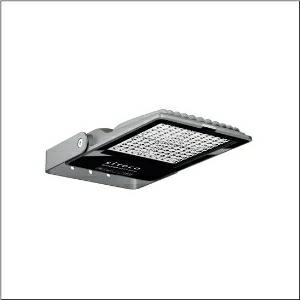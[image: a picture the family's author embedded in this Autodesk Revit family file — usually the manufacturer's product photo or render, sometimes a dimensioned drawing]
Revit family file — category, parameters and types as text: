
# Revit family: sicompact_r__31_mini___pl32_5xa7571b2k23_8fae
name_source: partatom
category: Lighting Fixtures
units: mm (PartAtom-declared; Revit-internal decimal feet)

## family parameters
Cut with Voids When Loaded = No
Host = Face
Light Source = No
Part Type = Normal
Room Calculation Point = No
Round Connector Dimension = Use Diameter
Shared = No

## types (1)
- SiCompact® 31 mini  PL32 (1 x LED, 8000 lm, 47 W, 4000K)
    Apparent Load = 47 VA
    CIE Flux Codes = 32 69 98 100 100
    Color Rendering = 70
    Color Temperature = 4000K
    Default Elevation = 1800 mm
    Description = SiCompact® 31 mini, floodlight, primary light control with lens, of plastic, of toughened safety glass, transparent, light distribution: PL32, light emission: direct distribution, primary light characteristic: asymmetric, installation type: surface-mounted, LED, High Power LED, rated luminous flux: 8.000lm, luminous efficacy: 170lm/W, light colour: 740, colour temperature: 4000K, control gear: ON/OFF, with cable, 3x 1.5mm², mains connection: 220..240V, AC, 50/60Hz, connection cable pre-assembled, cable length: 2m, rated input power: 47W, of diecast aluminium, specular, metallic grey (RAL 9006), length: 461mm, width: 261mm, height: 62mm, bracket, of sheet steel, coated, metallic grey (RAL 9006), ON/OFF, protection rating (complete): IP66, insulation class (complete): insulation class I (protective earthing), certification: CE, ENEC, impact resistance: IK08, permissible operating ambient temperature: -40..+45°C, packaging unit: 1 piece

Light Distribution: PL32
    Height = 62 mm
    Lamp = 1 x LED
    Lamp Light Flux = 8000 lm
    Lamp Power = 47 W
    Lamp count = 1
    Length = 460 mm
    Luminous efficacy = 170 lm/W
    Manufacturer = Siteco
    ModVariant = No
    Model = 5XA7571B2K23
    Mounting Place = Wall
    Mounting Type = Surface mounted
    Number of Poles = 1
    OnlyDefault = Yes
    Power Factor = 1
    Product Name = SiCompact® 31 mini | PL32
    Product group = floodlight | wall mounted
    ProductGroupID = 2001
    Protection Class = Protection class I
    Protection Degree = IP 66
    RLX_Detail_Level = 1
    RLX_Emergency_Light_Flux = 0 lm
    RLX_Emergency_Type = 0
    RLX_Emergency_Type_DB = No
    RlxData = <blob elided: 127105 chars, md5=e588fcea>
    Socket = socket
    Standby Power = 0 W
    System Light Flux = 8000 lm
    System Power = 47 W
    Type Comments = Product without accessories
    Type Image = l_1006951.jpg
    URL = http://relux.com
    VarID = ---
    Voltage = 0 V
    Weight = 0.00 kg
    Width = 260 mm

## geometry (parser evidence)
native form markers: Blend x4, Sweep x14
no freeform markers — native parametric forms only
